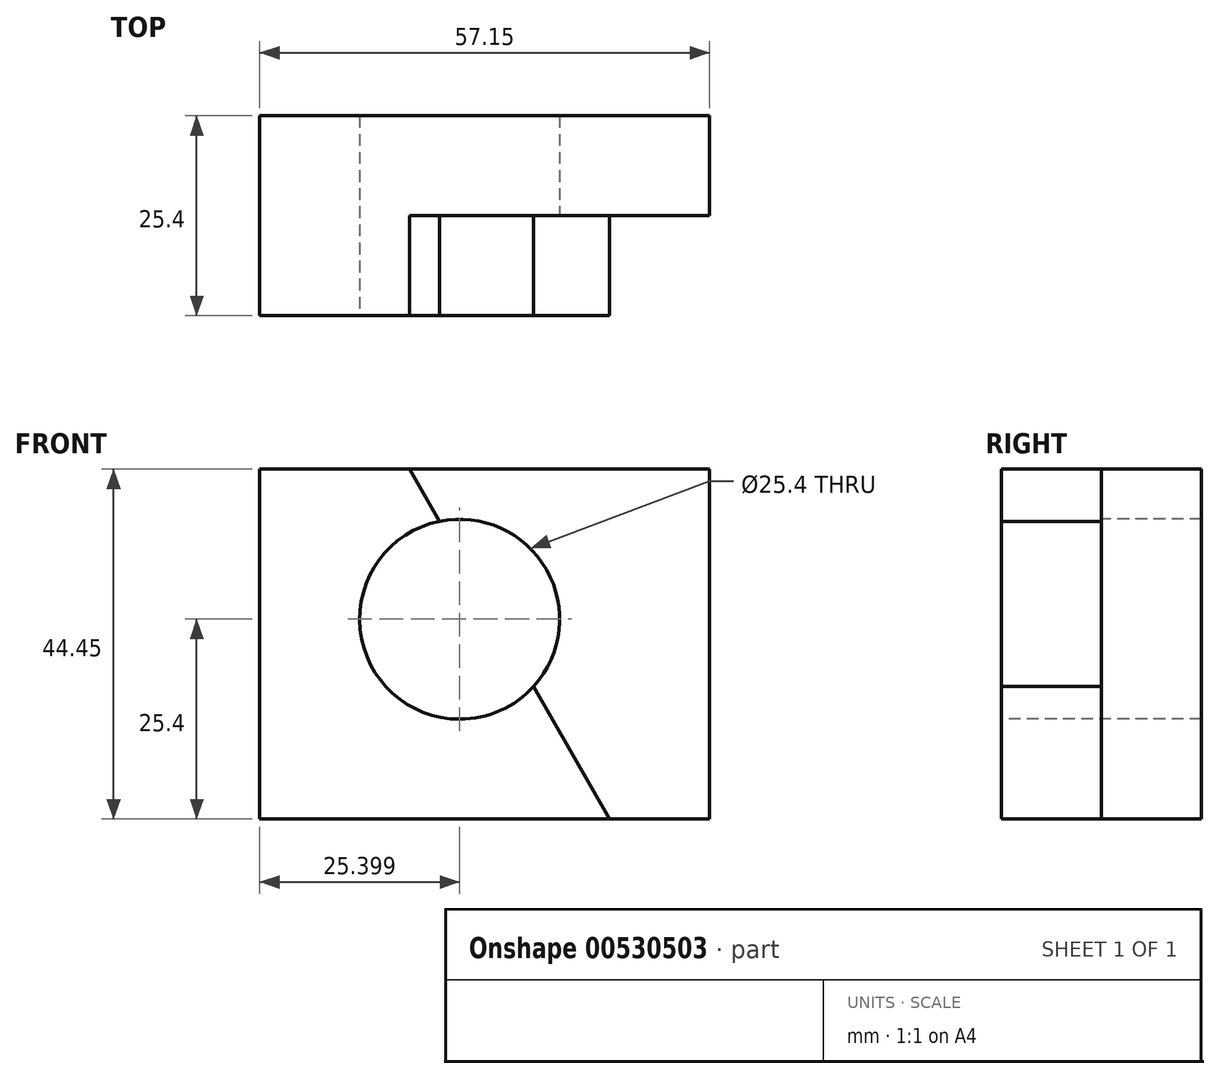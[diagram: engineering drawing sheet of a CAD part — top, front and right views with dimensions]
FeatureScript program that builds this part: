
annotation { "Feature Type Name" : "Feature", "Feature Type Description" : "" }
export const myFeature = defineFeature(function(context is Context, id is Id, definition is map)
    precondition{}
    {
        {
            var Q0;
            Q0=qCreatedBy(makeId("Front.planeOp"),FACE);
            var sketch = newSketch(context, id + "F0", { "sketchPlane" : qUnion([Q0])});
            skLineSegment(sketch, "E0.bottom", {"start": v(-64.68, 44.45) * mm, "end": v(-7.53, 44.45) * mm});
            skLineSegment(sketch, "E0.top", {"start": v(-64.68, 0) * mm, "end": v(-7.53, 0) * mm});
            skLineSegment(sketch, "E0.left", {"start": v(-64.68, 44.45) * mm, "end": v(-64.68, 0) * mm});
            skLineSegment(sketch, "E0.right", {"start": v(-7.53, 44.45) * mm, "end": v(-7.53, 0) * mm});
            skSolve(sketch);
        }
        {
            var Q0;
            Q0=makeQuery(id+"F0.imprint","IMPRINT",FACE,{"disambiguationData":[TD([[makeQuery(id+"F0.imprint","IMPRINT",EDGE,{"derivedFrom":sQuery(id+"F0.wireOp",EDGE,"E0.bottom")}),-1.0]])]});
            extrude(context, id + "F1", {"entities" : qUnion([Q0]), "depth" : 25.4 * mm, "offsetDistance" : 25.4 * mm});
        }
        {
            var Q0;
            Q0=makeQuery(id+"F1.opExtrude","CAP_FACE",FACE,{"disambiguationData":[OSD([sQuery(id+"F0.wireOp",EDGE,"E0.bottom"),sQuery(id+"F0.wireOp",EDGE,"E0.top"),sQuery(id+"F0.wireOp",EDGE,"E0.left"),sQuery(id+"F0.wireOp",EDGE,"E0.right")])],"isStart":false});
            var sketch = newSketch(context, id + "F2", { "sketchPlane" : qUnion([Q0])});
            skCircle(sketch, "E1", {"center": v(-39.28, 25.4) * mm, "radius": 12.7 * mm});
            skSolve(sketch);
        }
        {
            var Q0;
            Q0=makeQuery(id+"F2.imprint","IMPRINT",FACE,{"disambiguationData":[TD([[makeQuery(id+"F2.imprint","IMPRINT",EDGE,{"derivedFrom":sQuery(id+"F2.wireOp",EDGE,"E1")}),1.0]])]});
            extrude(context, id + "F3", {"entities" : qUnion([Q0]), "operationType" : NewBodyOperationType.REMOVE, "endBound" : BoundingType.THROUGH_ALL, "oppositeDirection" : true, "depth" : 25.4 * mm, "offsetDistance" : 25.4 * mm});
        }
        {
            var Q0;
            Q0=makeQuery(id+"F1.opExtrude","CAP_FACE",FACE,{"disambiguationData":[OSD([sQuery(id+"F0.wireOp",EDGE,"E0.bottom"),sQuery(id+"F0.wireOp",EDGE,"E0.top"),sQuery(id+"F0.wireOp",EDGE,"E0.left"),sQuery(id+"F0.wireOp",EDGE,"E0.right")])],"isStart":false});
            var sketch = newSketch(context, id + "F4", { "sketchPlane" : qUnion([Q0])});
            skLineSegment(sketch, "E2", {"start": v(-45.63, 44.45) * mm, "end": v(-20.23, 0) * mm});
            skLineSegment(sketch, "E3", {"start": v(-45.63, 44.45) * mm, "end": v(-7.53, 44.45) * mm});
            skLineSegment(sketch, "E4", {"start": v(-7.53, 44.45) * mm, "end": v(-7.53, 0) * mm});
            skLineSegment(sketch, "E5", {"start": v(-7.53, 0) * mm, "end": v(-20.23, 0) * mm});
            skSolve(sketch);
        }
        {
            var Q0;
            {var subQ0=sQuery(id+"F4.wireOp",EDGE,"E2");var subQ1=makeQuery(id+"F3.boolean.opBoolean","COPY",EDGE,{"derivedFrom":makeQuery(id+"F3.opExtrude","CAP_EDGE",EDGE,{"disambiguationData":[OSD([sQuery(id+"F2.wireOp",EDGE,"E1")])],"isStart":true})});var subQ2=makeQuery(id+"F4.imprint","INTERSECT",VERTEX,{"disambiguationData":[OD(0.0)],"derivedFrom":[subQ1,subQ0]});Q0=makeQuery(id+"F4.imprint","IMPRINT",FACE,{"disambiguationData":[TD([[makeQuery(id+"F4.imprint","IMPRINT",EDGE,{"disambiguationData":[TD([[subQ2,-1.0]])],"derivedFrom":subQ0}),1.0]])]});}
            var Q1;
            {var subQ0=sQuery(id+"F4.wireOp",EDGE,"E3");Q1=makeQuery(id+"F4.imprint","IMPRINT",FACE,{"disambiguationData":[TD([[makeQuery(id+"F4.imprint","IMPRINT",EDGE,{"derivedFrom":subQ0}),-1.0]])]});}
            extrude(context, id + "F5", {"entities" : qUnion([Q0, Q1]), "operationType" : NewBodyOperationType.REMOVE, "oppositeDirection" : true, "depth" : 12.7 * mm, "offsetDistance" : 25.4 * mm});
        }
    });
